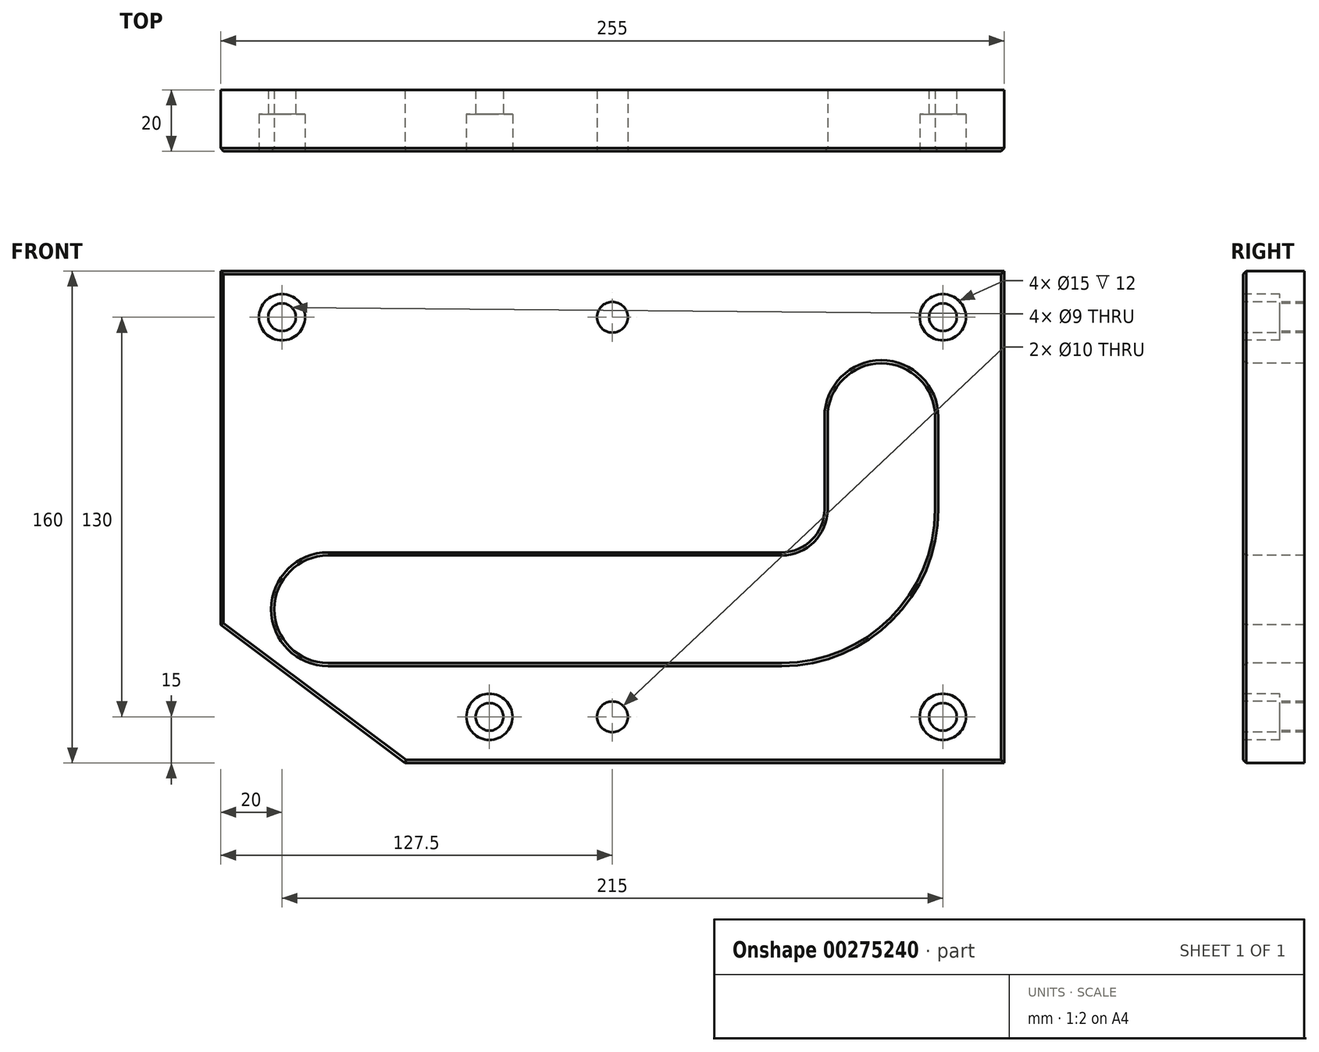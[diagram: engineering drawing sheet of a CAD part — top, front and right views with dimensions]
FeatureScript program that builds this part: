
annotation { "Feature Type Name" : "Feature", "Feature Type Description" : "" }
export const myFeature = defineFeature(function(context is Context, id is Id, definition is map)
    precondition{}
    {
        {
            var Q0;
            Q0=qCreatedBy(makeId("Front.planeOp"),FACE);
            var sketch = newSketch(context, id + "F0", { "sketchPlane" : qUnion([Q0])});
            skLineSegment(sketch, "E0.bottom", {"start": v(0, 0) * mm, "end": v(255, 0) * mm});
            skLineSegment(sketch, "E0.top", {"start": v(0, 160) * mm, "end": v(255, 160) * mm});
            skLineSegment(sketch, "E0.left", {"start": v(0, 0) * mm, "end": v(0, 160) * mm});
            skLineSegment(sketch, "E0.right", {"start": v(255, 0) * mm, "end": v(255, 160) * mm});
            skLineSegment(sketch, "E1", {"start": v(0, 45) * mm, "end": v(60, 0) * mm});
            skArc(sketch, "E2", {"start": v(35, 67.5) * mm, "mid": v(17.5, 50) * mm, "end": v(35, 32.5) * mm});
            skArc(sketch, "E3", {"start": v(232.5, 112.5) * mm, "mid": v(215, 130) * mm, "end": v(197.5, 112.5) * mm});
            skLineSegment(sketch, "E4", {"start": v(35, 67.5) * mm, "end": v(182.5, 67.5) * mm});
            skLineSegment(sketch, "E5", {"start": v(35, 32.5) * mm, "end": v(182.5, 32.5) * mm});
            skLineSegment(sketch, "E6", {"start": v(197.5, 112.5) * mm, "end": v(197.5, 82.5) * mm});
            skLineSegment(sketch, "E7", {"start": v(232.5, 112.5) * mm, "end": v(232.5, 82.5) * mm});
            skArc(sketch, "E8", {"start": v(182.5, 67.5) * mm, "mid": v(193.1, 71.9) * mm, "end": v(197.5, 82.5) * mm});
            skArc(sketch, "E9", {"start": v(182.5, 32.5) * mm, "mid": v(217.86, 47.14) * mm, "end": v(232.5, 82.5) * mm});
            skCircle(sketch, "E10", {"center": v(127.5, 145) * mm, "radius": 5 * mm});
            skCircle(sketch, "E11", {"center": v(127.5, 15) * mm, "radius": 5 * mm});
            skSolve(sketch);
        }
        {
            var Q0;
            {var subQ2=sQuery(id+"F0.wireOp",EDGE,"E0.top");Q0=makeQuery(id+"F0.imprint","IMPRINT",FACE,{"disambiguationData":[TD([[makeQuery(id+"F0.imprint","IMPRINT",EDGE,{"derivedFrom":subQ2}),-1.0]])]});}
            extrude(context, id + "F1", {"entities" : qUnion([Q0]), "oppositeDirection" : true, "depth" : 20 * mm});
        }
        {
            var Q0;
            Q0=makeQuery(id+"F1.opExtrude","CAP_FACE",FACE,{"disambiguationData":[OSD([sQuery(id+"F0.wireOp",EDGE,"E0.bottom"),sQuery(id+"F0.wireOp",EDGE,"E0.top"),sQuery(id+"F0.wireOp",EDGE,"E0.left"),sQuery(id+"F0.wireOp",EDGE,"E0.right"),sQuery(id+"F0.wireOp",EDGE,"E1"),sQuery(id+"F0.wireOp",EDGE,"E2"),sQuery(id+"F0.wireOp",EDGE,"E3"),sQuery(id+"F0.wireOp",EDGE,"E4"),sQuery(id+"F0.wireOp",EDGE,"E5"),sQuery(id+"F0.wireOp",EDGE,"E6"),sQuery(id+"F0.wireOp",EDGE,"E7"),sQuery(id+"F0.wireOp",EDGE,"E8"),sQuery(id+"F0.wireOp",EDGE,"E9"),sQuery(id+"F0.wireOp",EDGE,"E10"),sQuery(id+"F0.wireOp",EDGE,"E11")])],"isStart":true});
            var sketch = newSketch(context, id + "F2", { "sketchPlane" : qUnion([Q0])});
            skCircle(sketch, "E12", {"center": v(235, 15) * mm, "radius": 7.5 * mm});
            skCircle(sketch, "E13", {"center": v(235, 15) * mm, "radius": 4.5 * mm});
            skCircle(sketch, "E14", {"center": v(235, 145) * mm, "radius": 7.5 * mm});
            skCircle(sketch, "E15", {"center": v(235, 145) * mm, "radius": 4.5 * mm});
            skCircle(sketch, "E16", {"center": v(20, 145) * mm, "radius": 7.5 * mm});
            skCircle(sketch, "E17", {"center": v(20, 145) * mm, "radius": 4.5 * mm});
            skCircle(sketch, "E18", {"center": v(87.5, 15) * mm, "radius": 7.5 * mm});
            skCircle(sketch, "E19", {"center": v(87.5, 15) * mm, "radius": 4.5 * mm});
            skCircle(sketch, "E20.0", {"center": v(127.5, 15) * mm, "radius": 5 * mm});
            skSolve(sketch);
        }
        {
            var Q0;
            Q0=makeQuery(id+"F2.imprint","IMPRINT",FACE,{"disambiguationData":[TD([[makeQuery(id+"F2.imprint","IMPRINT",EDGE,{"derivedFrom":sQuery(id+"F2.wireOp",EDGE,"E16")}),1.0]])]});
            var Q1;
            Q1=makeQuery(id+"F2.imprint","IMPRINT",FACE,{"disambiguationData":[TD([[makeQuery(id+"F2.imprint","IMPRINT",EDGE,{"derivedFrom":sQuery(id+"F2.wireOp",EDGE,"E14")}),1.0]])]});
            var Q2;
            Q2=makeQuery(id+"F2.imprint","IMPRINT",FACE,{"disambiguationData":[TD([[makeQuery(id+"F2.imprint","IMPRINT",EDGE,{"derivedFrom":sQuery(id+"F2.wireOp",EDGE,"E12")}),1.0]])]});
            var Q3;
            Q3=makeQuery(id+"F2.imprint","IMPRINT",FACE,{"disambiguationData":[TD([[makeQuery(id+"F2.imprint","IMPRINT",EDGE,{"derivedFrom":sQuery(id+"F2.wireOp",EDGE,"E18")}),1.0]])]});
            extrude(context, id + "F3", {"entities" : qUnion([Q0, Q1, Q2, Q3]), "operationType" : NewBodyOperationType.REMOVE, "oppositeDirection" : true, "depth" : 12 * mm});
        }
        {
            var Q0;
            Q0=makeQuery(id+"F2.imprint","IMPRINT",FACE,{"disambiguationData":[TD([[makeQuery(id+"F2.imprint","IMPRINT",EDGE,{"derivedFrom":sQuery(id+"F2.wireOp",EDGE,"E17")}),1.0]])]});
            var Q1;
            Q1=makeQuery(id+"F2.imprint","IMPRINT",FACE,{"disambiguationData":[TD([[makeQuery(id+"F2.imprint","IMPRINT",EDGE,{"derivedFrom":sQuery(id+"F2.wireOp",EDGE,"E15")}),1.0]])]});
            var Q2;
            Q2=makeQuery(id+"F2.imprint","IMPRINT",FACE,{"disambiguationData":[TD([[makeQuery(id+"F2.imprint","IMPRINT",EDGE,{"derivedFrom":sQuery(id+"F2.wireOp",EDGE,"E19")}),1.0]])]});
            var Q3;
            Q3=makeQuery(id+"F2.imprint","IMPRINT",FACE,{"disambiguationData":[TD([[makeQuery(id+"F2.imprint","IMPRINT",EDGE,{"derivedFrom":sQuery(id+"F2.wireOp",EDGE,"E13")}),1.0]])]});
            extrude(context, id + "F4", {"entities" : qUnion([Q0, Q1, Q2, Q3]), "operationType" : NewBodyOperationType.REMOVE, "oppositeDirection" : true, "depth" : 25 * mm});
        }
        {
            var Q0;
            Q0=makeQuery(id+"F1.opExtrude","CAP_EDGE",EDGE,{"disambiguationData":[OSD([sQuery(id+"F0.wireOp",EDGE,"E0.bottom")])],"isStart":true});
            var Q1;
            Q1=makeQuery(id+"F1.opExtrude","CAP_EDGE",EDGE,{"disambiguationData":[OSD([sQuery(id+"F0.wireOp",EDGE,"E0.right")])],"isStart":true});
            var Q2;
            Q2=makeQuery(id+"F1.opExtrude","CAP_EDGE",EDGE,{"disambiguationData":[OSD([sQuery(id+"F0.wireOp",EDGE,"E0.top")])],"isStart":true});
            var Q3;
            Q3=makeQuery(id+"F1.opExtrude","CAP_EDGE",EDGE,{"disambiguationData":[OSD([sQuery(id+"F0.wireOp",EDGE,"E0.left")])],"isStart":true});
            var Q4;
            Q4=makeQuery(id+"F1.opExtrude","CAP_EDGE",EDGE,{"disambiguationData":[OSD([sQuery(id+"F0.wireOp",EDGE,"E1")])],"isStart":true});
            var Q5;
            Q5=makeQuery(id+"F1.opExtrude","CAP_EDGE",EDGE,{"disambiguationData":[OSD([sQuery(id+"F0.wireOp",EDGE,"E4")])],"isStart":true});
            var Q6;
            Q6=makeQuery(id+"F1.opExtrude","CAP_EDGE",EDGE,{"disambiguationData":[OSD([sQuery(id+"F0.wireOp",EDGE,"E2")])],"isStart":true});
            var Q7;
            Q7=makeQuery(id+"F1.opExtrude","CAP_EDGE",EDGE,{"disambiguationData":[OSD([sQuery(id+"F0.wireOp",EDGE,"E5")])],"isStart":true});
            var Q8;
            Q8=makeQuery(id+"F1.opExtrude","CAP_EDGE",EDGE,{"disambiguationData":[OSD([sQuery(id+"F0.wireOp",EDGE,"E9")])],"isStart":true});
            chamfer(context, id + "F5", {"entities" : qUnion([Q0, Q1, Q2, Q3, Q4, Q5, Q6, Q7, Q8]), "chamferType" : ChamferType.OFFSET_ANGLE, "width" : 1 * mm, "oppositeDirection" : false, "angle" : 45 * degree, "tangentPropagation" : true});
        }
    });
